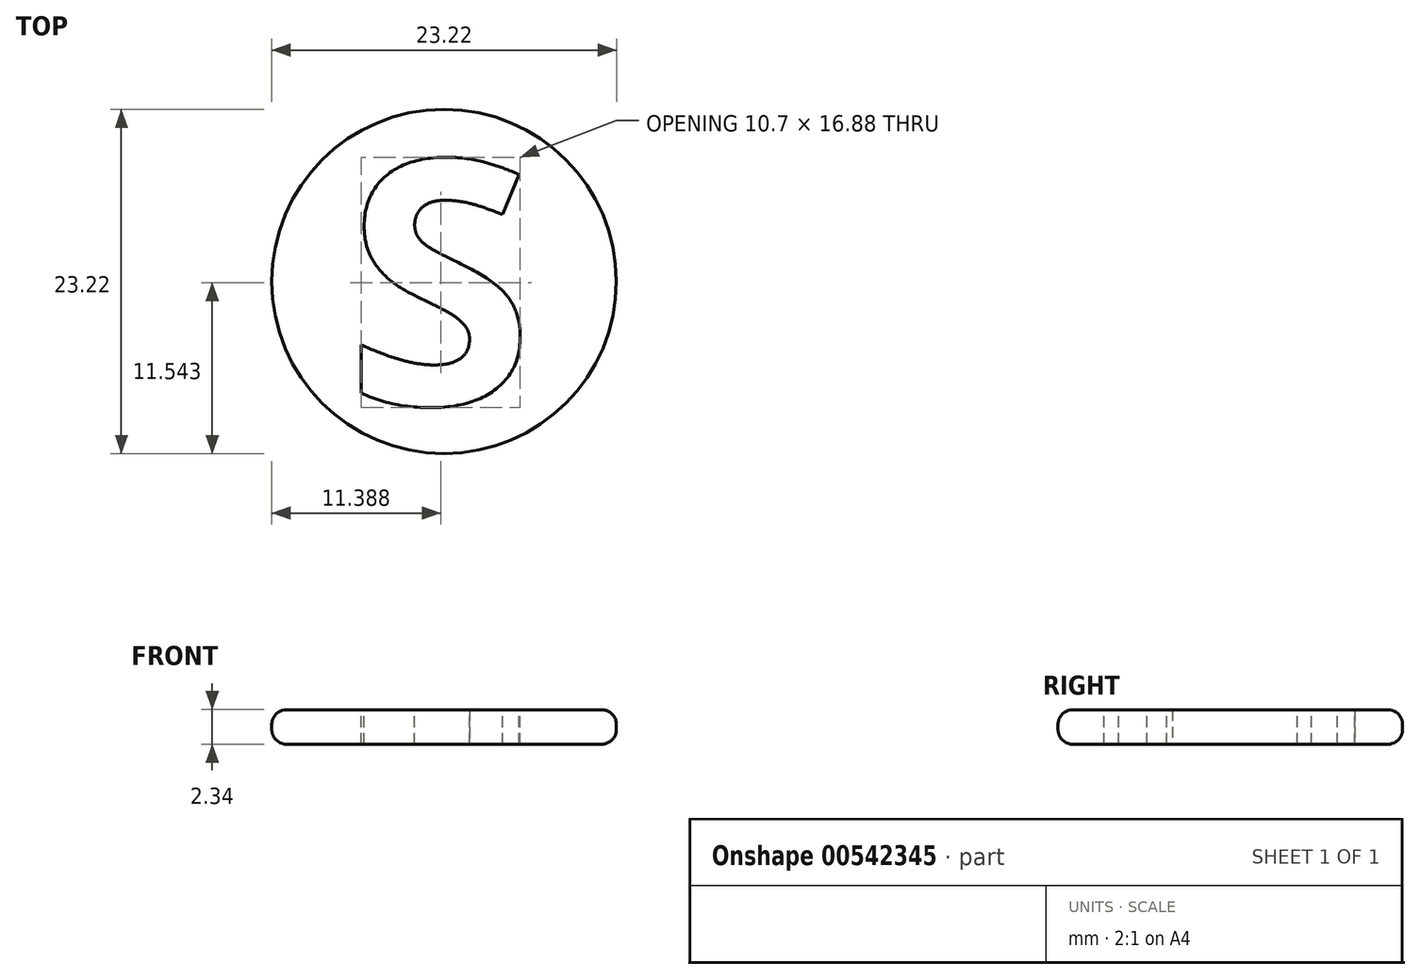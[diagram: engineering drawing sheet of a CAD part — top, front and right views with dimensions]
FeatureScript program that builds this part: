
annotation { "Feature Type Name" : "Feature", "Feature Type Description" : "" }
export const myFeature = defineFeature(function(context is Context, id is Id, definition is map)
    precondition{}
    {
        {
            var Q0;
            Q0=qCreatedBy(makeId("Top.planeOp"),FACE);
            var sketch = newSketch(context, id + "F0", { "sketchPlane" : qUnion([Q0])});
            skCircle(sketch, "E0", {"center": v(0, 0) * mm, "radius": 11.6 * mm});
            skSolve(sketch);
        }
        {
            var Q0;
            Q0 = qSketchRegion(id + "F0", true);
            extrude(context, id + "F1", {"entities" : qUnion([Q0]), "endBound" : BoundingType.SYMMETRIC, "depth" : 2.33 * mm, "offsetDistance" : 25 * mm});
        }
        {
            var Q0;
            Q0=makeQuery(id+"F1.opExtrude","CAP_EDGE",EDGE,{"disambiguationData":[OSD([sQuery(id+"F0.wireOp",EDGE,"E0")])],"isStart":false});
            var Q1;
            Q1=makeQuery(id+"F1.opExtrude","CAP_EDGE",EDGE,{"disambiguationData":[OSD([sQuery(id+"F0.wireOp",EDGE,"E0")])],"isStart":true});
            fillet(context, id + "F2", {"entities" : qUnion([Q0, Q1]), "radius" : 1 * mm, "tangentPropagation" : true, "allowEdgeOverflow" : false});
        }
        {
            var Q0;
            Q0=makeQuery(id+"F1.opExtrude","CAP_FACE",FACE,{"disambiguationData":[OSD([sQuery(id+"F0.wireOp",EDGE,"E0")])],"isStart":false});
            var sketch = newSketch(context, id + "F3", { "sketchPlane" : qUnion([Q0])});
            skText(sketch, "E1", { "text": "S", "fontName": "OpenSans-Bold.ttf"});
            const initialGuessF3  = {"E1": [-0.00663, -0.00828, 1, 0, 0.01656]};
            skSetInitialGuess(sketch, initialGuessF3);
            skSolve(sketch);
        }
        {
            var Q0;
            Q0 = qSketchRegion(id + "F3", true);
            extrude(context, id + "F4", {"entities" : qUnion([Q0]), "operationType" : NewBodyOperationType.REMOVE, "endBound" : BoundingType.THROUGH_ALL, "oppositeDirection" : true, "depth" : 1 * mm, "offsetDistance" : 25 * mm});
        }
    });
